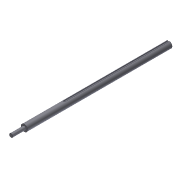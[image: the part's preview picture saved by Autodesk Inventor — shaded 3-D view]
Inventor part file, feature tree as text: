
AUTODESK INVENTOR PART (.ipt)
format: ipt  version: 2012 (Build 160160000, 160)  size: 84,480 bytes
history: native  units: in
note: dims shown in document units (in); Inventor stores cm internally (conversion verified against a paired STEP export)
features: extrude x3, sketch x3
ambient origin geometry x8: Origin, YZ Plane, XZ Plane, XY Plane, X Axis, Y Axis, Z Axis, Center Point
bodies: Solid1 (feature_tree)
feature tree (6):
  extrude  "Extrusion1"  Depth=12.0in TaperAngle=0.0deg
  extrude  "Extrusion2"  Depth=1.0in TaperAngle=0.0deg
  extrude  "Extrusion3"  Depth=0.0625in
  sketch  "Sketch1"  dims[d0=0.5in d1=12.0in d2=0.0in]
  sketch  "Sketch2"  dims[d3=0.27in d4=1.0in d5=0.0in]
  sketch  "Sketch3"  dims[d6=0.125in d7=0.0625in d8=8.0in d9=0.0in]
